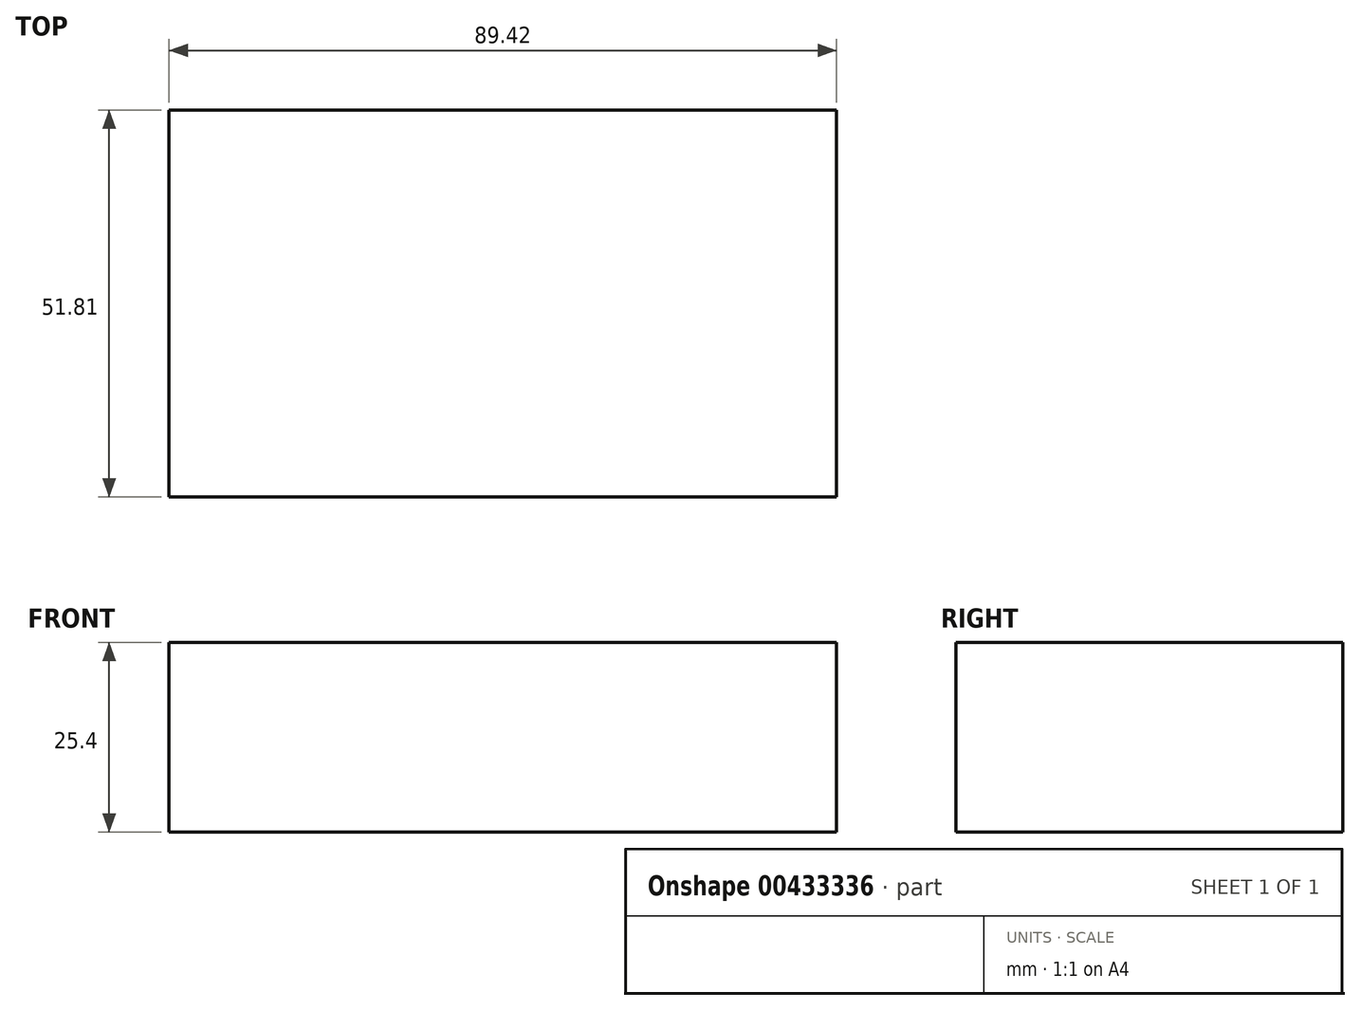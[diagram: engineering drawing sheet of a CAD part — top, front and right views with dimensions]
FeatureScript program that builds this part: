
annotation { "Feature Type Name" : "Feature", "Feature Type Description" : "" }
export const myFeature = defineFeature(function(context is Context, id is Id, definition is map)
    precondition{}
    {
        {
            var Q0;
            Q0=qCreatedBy(makeId("Top.planeOp"),FACE);
            var sketch = newSketch(context, id + "F0", { "sketchPlane" : qUnion([Q0])});
            skLineSegment(sketch, "E0.bottom", {"start": v(-40, 24.89) * mm, "end": v(49.4, 24.89) * mm});
            skLineSegment(sketch, "E0.top", {"start": v(-40, -26.92) * mm, "end": v(49.4, -26.92) * mm});
            skLineSegment(sketch, "E0.left", {"start": v(-40, 24.89) * mm, "end": v(-40, -26.92) * mm});
            skLineSegment(sketch, "E0.right", {"start": v(49.4, 24.89) * mm, "end": v(49.4, -26.92) * mm});
            skSolve(sketch);
        }
        {
            var Q0;
            Q0=makeQuery(id+"F0.imprint","IMPRINT",FACE,{"disambiguationData":[TD([[makeQuery(id+"F0.imprint","IMPRINT",EDGE,{"derivedFrom":sQuery(id+"F0.wireOp",EDGE,"E0.bottom")}),-1.0]])]});
            extrude(context, id + "F1", {"entities" : qUnion([Q0]), "depth" : 25.4 * mm});
        }
    });
